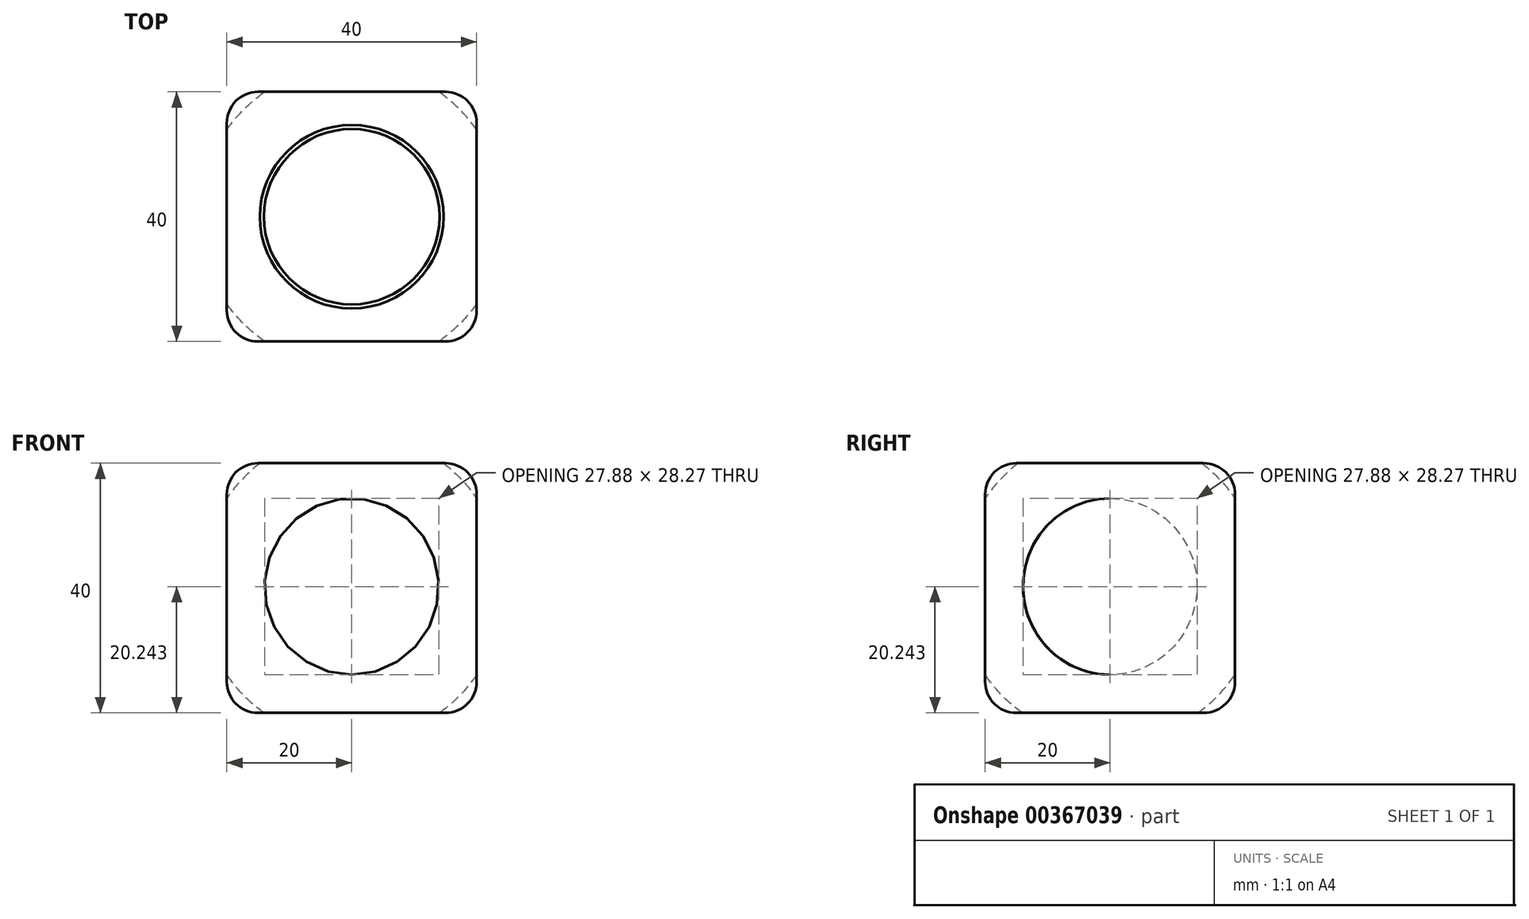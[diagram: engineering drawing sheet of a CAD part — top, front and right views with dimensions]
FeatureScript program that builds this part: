
annotation { "Feature Type Name" : "Feature", "Feature Type Description" : "" }
export const myFeature = defineFeature(function(context is Context, id is Id, definition is map)
    precondition{}
    {
        {
            var Q0;
            Q0=qCreatedBy(makeId("Top.planeOp"),FACE);
            var sketch = newSketch(context, id + "F0", { "sketchPlane" : qUnion([Q0])});
            skLineSegment(sketch, "E0.bottom", {"start": v(20, 20) * mm, "end": v(-20, 20) * mm});
            skLineSegment(sketch, "E0.top", {"start": v(20, -20) * mm, "end": v(-20, -20) * mm});
            skLineSegment(sketch, "E0.left", {"start": v(20, 20) * mm, "end": v(20, -20) * mm});
            skLineSegment(sketch, "E0.right", {"start": v(-20, 20) * mm, "end": v(-20, -20) * mm});
            skPoint(sketch, "E0.middle", {"position": v(0, 0) * mm});
            skSolve(sketch);
        }
        {
            var Q0;
            Q0 = qSketchRegion(id + "F0", true);
            extrude(context, id + "F1", {"entities" : qUnion([Q0]), "depth" : 40 * mm});
        }
        {
            var Q0;
            Q0=qCreatedBy(makeId("Front.planeOp"),FACE);
            var sketch = newSketch(context, id + "F2", { "sketchPlane" : qUnion([Q0])});
            skLineSegment(sketch, "E1", {"start": v(0, 45.24) * mm, "end": v(0, -4.76) * mm});
            skArc(sketch, "E2", {"start": v(0, -4.76) * mm, "mid": v(24.38, 20.24) * mm, "end": v(0, 45.24) * mm});
            skSolve(sketch);
        }
        {
            var Q0;
            Q0=makeQuery(id+"F2.imprint","IMPRINT",FACE,{"disambiguationData":[TD([[makeQuery(id+"F2.imprint","IMPRINT",EDGE,{"derivedFrom":sQuery(id+"F2.wireOp",EDGE,"E1")}),1.0]])]});
            var Q1;
            Q1=sQuery(id+"F2.wireOp",EDGE,"E1");
            revolve(context, id + "F3", {"operationType" : NewBodyOperationType.REMOVE, "entities" : qUnion([Q0]), "axis" : qUnion([Q1]), "revolveType" : RevolveType.FULL});
        }
        {
            var Q0;
            Q0=makeQuery(id+"F1.opExtrude","CAP_EDGE",EDGE,{"disambiguationData":[OSD([sQuery(id+"F0.wireOp",EDGE,"E0.right")])],"isStart":false});
            var Q1;
            Q1=makeQuery(id+"F1.opExtrude","SWEPT_EDGE",EDGE,{"disambiguationData":[OSD([sQuery(id+"F0.wireOp",EDGE,"E0.top"),sQuery(id+"F0.wireOp",EDGE,"E0.right")])]});
            var Q2;
            Q2=makeQuery(id+"F1.opExtrude","CAP_EDGE",EDGE,{"disambiguationData":[OSD([sQuery(id+"F0.wireOp",EDGE,"E0.top")])],"isStart":false});
            var Q3;
            Q3=makeQuery(id+"F1.opExtrude","CAP_EDGE",EDGE,{"disambiguationData":[OSD([sQuery(id+"F0.wireOp",EDGE,"E0.top")])],"isStart":true});
            var Q4;
            Q4=makeQuery(id+"F1.opExtrude","CAP_EDGE",EDGE,{"disambiguationData":[OSD([sQuery(id+"F0.wireOp",EDGE,"E0.right")])],"isStart":true});
            var Q5;
            Q5=makeQuery(id+"F1.opExtrude","CAP_EDGE",EDGE,{"disambiguationData":[OSD([sQuery(id+"F0.wireOp",EDGE,"E0.bottom")])],"isStart":true});
            var Q6;
            Q6=makeQuery(id+"F1.opExtrude","SWEPT_EDGE",EDGE,{"disambiguationData":[OSD([sQuery(id+"F0.wireOp",EDGE,"E0.bottom"),sQuery(id+"F0.wireOp",EDGE,"E0.right")])]});
            var Q7;
            Q7=makeQuery(id+"F1.opExtrude","CAP_EDGE",EDGE,{"disambiguationData":[OSD([sQuery(id+"F0.wireOp",EDGE,"E0.left")])],"isStart":true});
            var Q8;
            Q8=makeQuery(id+"F1.opExtrude","SWEPT_EDGE",EDGE,{"disambiguationData":[OSD([sQuery(id+"F0.wireOp",EDGE,"E0.bottom"),sQuery(id+"F0.wireOp",EDGE,"E0.left")])]});
            var Q9;
            Q9=makeQuery(id+"F1.opExtrude","SWEPT_EDGE",EDGE,{"disambiguationData":[OSD([sQuery(id+"F0.wireOp",EDGE,"E0.top"),sQuery(id+"F0.wireOp",EDGE,"E0.left")])]});
            var Q10;
            Q10=makeQuery(id+"F1.opExtrude","CAP_EDGE",EDGE,{"disambiguationData":[OSD([sQuery(id+"F0.wireOp",EDGE,"E0.left")])],"isStart":false});
            var Q11;
            Q11=makeQuery(id+"F1.opExtrude","CAP_EDGE",EDGE,{"disambiguationData":[OSD([sQuery(id+"F0.wireOp",EDGE,"E0.bottom")])],"isStart":false});
            fillet(context, id + "F4", {"entities" : qUnion([Q0, Q1, Q2, Q3, Q4, Q5, Q6, Q7, Q8, Q9, Q10, Q11]), "radius" : 5 * mm, "tangentPropagation" : true, "allowEdgeOverflow" : false});
        }
    });
